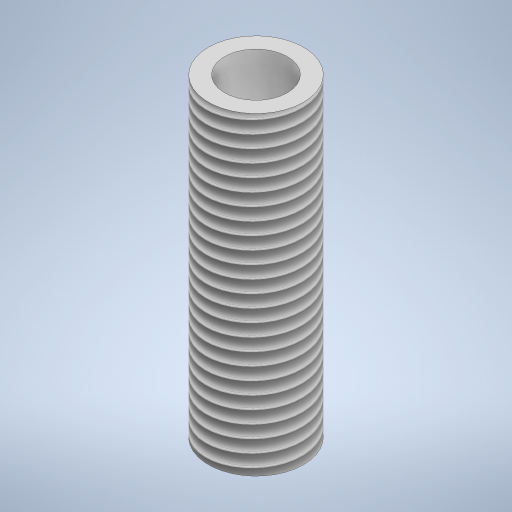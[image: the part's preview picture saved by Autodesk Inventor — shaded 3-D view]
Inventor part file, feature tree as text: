
AUTODESK INVENTOR PART (.ipt)
format: ipt  version: 2024 (Build 280153000, 153)  size: 311,808 bytes
history: native  units: mm
features: other x3, extrude x1, thread x1, hole x1
ambient origin geometry x8: Origin, YZ Plane, XZ Plane, XY Plane, X Axis, Y Axis, Z Axis, Center Point
bodies: Body1 (feature_tree)
feature tree (6):
  other  "Sólido1"
  extrude  "Extrusión1"  Depth=15.164mm
  thread  "Rosca1"  [1 undecoded]
  hole  "Agujero1"  [1 undecoded]
  other  "Edición directa1"
  other  "Escala1"
note: 2 required parameter values undecoded (feature->parameter linkage not recoverable at this tier; creation-order binding heuristic only, values carry confidence <= 0.55)
